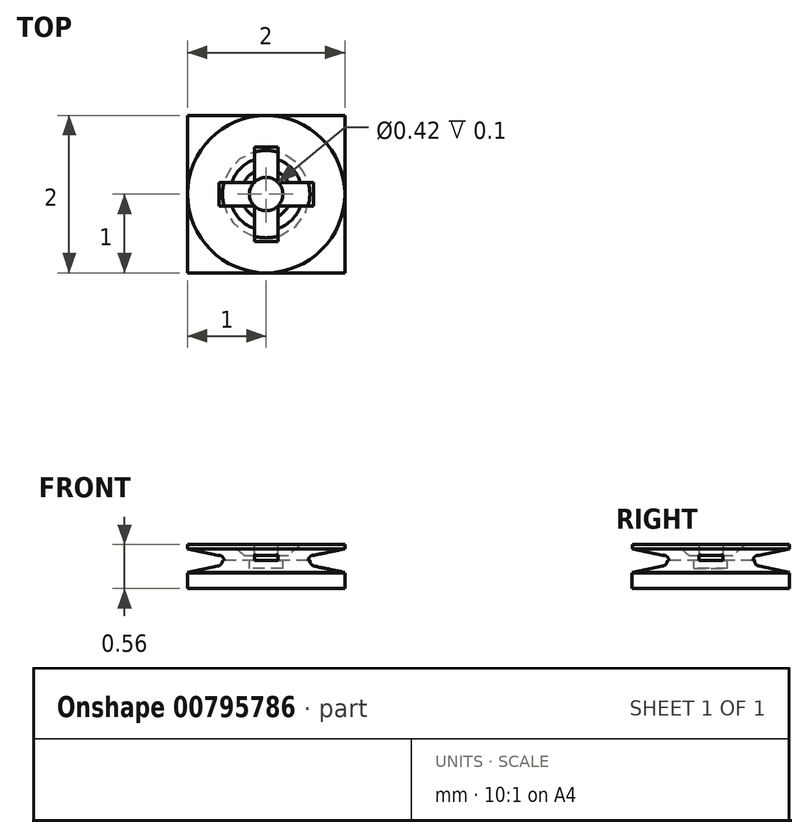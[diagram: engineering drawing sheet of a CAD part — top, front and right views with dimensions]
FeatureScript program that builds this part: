
annotation { "Feature Type Name" : "Feature", "Feature Type Description" : "" }
export const myFeature = defineFeature(function(context is Context, id is Id, definition is map)
    precondition{}
    {
        {
            var Q0;
            Q0=qCreatedBy(makeId("Top.planeOp"),FACE);
            var sketch = newSketch(context, id + "F0", { "sketchPlane" : qUnion([Q0])});
            skLineSegment(sketch, "E0.bottom", {"start": v(1, -1) * mm, "end": v(-1, -1) * mm});
            skLineSegment(sketch, "E0.top", {"start": v(1, 1) * mm, "end": v(-1, 1) * mm});
            skLineSegment(sketch, "E0.left", {"start": v(1, -1) * mm, "end": v(1, 1) * mm});
            skLineSegment(sketch, "E0.right", {"start": v(-1, -1) * mm, "end": v(-1, 1) * mm});
            skPoint(sketch, "E0.middle", {"position": v(0, 0) * mm});
            skSolve(sketch);
        }
        {
            var Q0;
            Q0 = qSketchRegion(id + "F0", true);
            extrude(context, id + "F1", {"entities" : qUnion([Q0]), "depth" : 0.2 * mm, "offsetDistance" : 25 * mm});
        }
        {
            var Q0;
            Q0=qCreatedBy(makeId("Right.planeOp"),FACE);
            var sketch = newSketch(context, id + "F2", { "sketchPlane" : qUnion([Q0])});
            skLineSegment(sketch, "E1", {"start": v(-1, 0.2) * mm, "end": v(-0.61, 0.28) * mm});
            skArc(sketch, "E2", {"start": v(-0.61, 0.28) * mm, "mid": v(-0.55, 0.35) * mm, "end": v(-0.61, 0.42) * mm});
            skLineSegment(sketch, "E3", {"start": v(-0.32, 0.42) * mm, "end": v(0, 0.42) * mm});
            skLineSegment(sketch, "E4", {"start": v(0, 0.42) * mm, "end": v(0, 0.2) * mm});
            skLineSegment(sketch, "E5", {"start": v(0, 0.2) * mm, "end": v(-1, 0.2) * mm});
            skLineSegment(sketch, "E6", {"start": v(-0.61, 0.42) * mm, "end": v(-1, 0.5) * mm});
            skLineSegment(sketch, "E7", {"start": v(-1, 0.5) * mm, "end": v(-1, 0.56) * mm});
            skLineSegment(sketch, "E8", {"start": v(-1, 0.56) * mm, "end": v(-0.46, 0.56) * mm});
            skLineSegment(sketch, "E9", {"start": v(-0.32, 0.42) * mm, "end": v(-0.46, 0.56) * mm});
            skSolve(sketch);
        }
        {
            var Q0;
            Q0=makeQuery(id+"F2.imprint","IMPRINT",FACE,{"disambiguationData":[TD([[makeQuery(id+"F2.imprint","IMPRINT",EDGE,{"derivedFrom":sQuery(id+"F2.wireOp",EDGE,"E1")}),-1.0]])]});
            var Q1;
            Q1=sQuery(id+"F2.wireOp",EDGE,"E4");
            revolve(context, id + "F3", {"surfaceOperationType" : NewSurfaceOperationType.NEW, "entities" : qUnion([Q0]), "axis" : qUnion([Q1]), "revolveType" : RevolveType.FULL});
        }
        {
            var Q0;
            Q0=makeQuery(id+"F3.opRevolve","SWEPT_FACE",FACE,{"disambiguationData":[OSD([sQuery(id+"F2.wireOp",EDGE,"E8")])]});
            var sketch = newSketch(context, id + "F4", { "sketchPlane" : qUnion([Q0])});
            skLineSegment(sketch, "E10.bottom", {"start": v(0.6, 0.15) * mm, "end": v(-0.6, 0.15) * mm});
            skLineSegment(sketch, "E10.top", {"start": v(0.6, -0.15) * mm, "end": v(-0.6, -0.15) * mm});
            skLineSegment(sketch, "E10.left", {"start": v(0.6, 0.15) * mm, "end": v(0.6, -0.15) * mm});
            skLineSegment(sketch, "E10.right", {"start": v(-0.6, 0.15) * mm, "end": v(-0.6, -0.15) * mm});
            skPoint(sketch, "E10.middle", {"position": v(0, 0) * mm});
            skLineSegment(sketch, "E11.bottom", {"start": v(0.15, 0.6) * mm, "end": v(-0.15, 0.6) * mm});
            skLineSegment(sketch, "E11.top", {"start": v(0.15, -0.6) * mm, "end": v(-0.15, -0.6) * mm});
            skLineSegment(sketch, "E11.left", {"start": v(0.15, 0.6) * mm, "end": v(0.15, -0.6) * mm});
            skLineSegment(sketch, "E11.right", {"start": v(-0.15, 0.6) * mm, "end": v(-0.15, -0.6) * mm});
            skSolve(sketch);
        }
        {
            var Q0;
            {var subQ0=sQuery(id+"F4.wireOp",EDGE,"E11.top");Q0=makeQuery(id+"F4.imprint","IMPRINT",FACE,{"disambiguationData":[TD([[makeQuery(id+"F4.imprint","IMPRINT",EDGE,{"derivedFrom":subQ0}),-1.0]])]});}
            var Q1;
            {var subQ0=sQuery(id+"F4.wireOp",EDGE,"E11.left");var subQ1=sQuery(id+"F4.wireOp",EDGE,"E10.top");var subQ2=makeQuery(id+"F4.imprint","INTERSECT",VERTEX,{"derivedFrom":[subQ1,subQ0]});Q1=makeQuery(id+"F4.imprint","IMPRINT",FACE,{"disambiguationData":[TD([[makeQuery(id+"F4.imprint","IMPRINT",EDGE,{"disambiguationData":[TD([[subQ2,-1.0]])],"derivedFrom":subQ1}),1.0]])]});}
            var Q2;
            {var subQ0=sQuery(id+"F4.wireOp",EDGE,"E11.left");var subQ1=sQuery(id+"F4.wireOp",EDGE,"E10.bottom");var subQ2=makeQuery(id+"F4.imprint","INTERSECT",VERTEX,{"derivedFrom":[subQ1,subQ0]});Q2=makeQuery(id+"F4.imprint","IMPRINT",FACE,{"disambiguationData":[TD([[makeQuery(id+"F4.imprint","IMPRINT",EDGE,{"disambiguationData":[TD([[subQ2,-1.0]])],"derivedFrom":subQ1}),1.0]])]});}
            var Q3;
            {var subQ0=sQuery(id+"F4.wireOp",EDGE,"E11.left");var subQ1=sQuery(id+"F4.wireOp",EDGE,"E10.bottom");var subQ2=makeQuery(id+"F4.imprint","INTERSECT",VERTEX,{"derivedFrom":[subQ1,subQ0]});Q3=makeQuery(id+"F4.imprint","IMPRINT",FACE,{"disambiguationData":[TD([[makeQuery(id+"F4.imprint","IMPRINT",EDGE,{"disambiguationData":[TD([[subQ2,-1.0]])],"derivedFrom":subQ1}),-1.0]])]});}
            var Q4;
            {var subQ0=sQuery(id+"F4.wireOp",EDGE,"E11.bottom");Q4=makeQuery(id+"F4.imprint","IMPRINT",FACE,{"disambiguationData":[TD([[makeQuery(id+"F4.imprint","IMPRINT",EDGE,{"derivedFrom":subQ0}),1.0]])]});}
            var Q5;
            {var subQ0=sQuery(id+"F4.wireOp",EDGE,"E11.left");var subQ1=sQuery(id+"F4.wireOp",EDGE,"E10.bottom");var subQ2=makeQuery(id+"F4.imprint","INTERSECT",VERTEX,{"derivedFrom":[subQ1,subQ0]});Q5=makeQuery(id+"F4.imprint","IMPRINT",FACE,{"disambiguationData":[TD([[makeQuery(id+"F4.imprint","IMPRINT",EDGE,{"disambiguationData":[TD([[subQ2,-1.0]])],"derivedFrom":subQ0}),1.0]])]});}
            var Q6;
            {var subQ0=sQuery(id+"F4.wireOp",EDGE,"E10.left");Q6=makeQuery(id+"F4.imprint","IMPRINT",FACE,{"disambiguationData":[TD([[makeQuery(id+"F4.imprint","IMPRINT",EDGE,{"derivedFrom":subQ0}),-1.0]])]});}
            var Q7;
            {var subQ0=sQuery(id+"F4.wireOp",EDGE,"E10.right");Q7=makeQuery(id+"F4.imprint","IMPRINT",FACE,{"disambiguationData":[TD([[makeQuery(id+"F4.imprint","IMPRINT",EDGE,{"derivedFrom":subQ0}),1.0]])]});}
            var Q8;
            {var subQ0=sQuery(id+"F4.wireOp",EDGE,"E11.right");var subQ1=sQuery(id+"F4.wireOp",EDGE,"E10.bottom");var subQ2=makeQuery(id+"F4.imprint","INTERSECT",VERTEX,{"derivedFrom":[subQ1,subQ0]});Q8=makeQuery(id+"F4.imprint","IMPRINT",FACE,{"disambiguationData":[TD([[makeQuery(id+"F4.imprint","IMPRINT",EDGE,{"disambiguationData":[TD([[subQ2,-1.0]])],"derivedFrom":subQ0}),-1.0]])]});}
            extrude(context, id + "F5", {"entities" : qUnion([Q0, Q1, Q2, Q3, Q4, Q5, Q6, Q7, Q8]), "operationType" : NewBodyOperationType.REMOVE, "oppositeDirection" : true, "depth" : 0.2 * mm, "offsetDistance" : 25 * mm});
        }
        {
            var Q0;
            Q0=makeQuery(id+"F5.boolean.opBoolean","COPY",FACE,{"derivedFrom":makeQuery(id+"F5.opExtrude","CAP_FACE",FACE,{"disambiguationData":[OSD([sQuery(id+"F4.wireOp",EDGE,"E10.bottom"),sQuery(id+"F4.wireOp",EDGE,"E10.top"),sQuery(id+"F4.wireOp",EDGE,"E10.left"),sQuery(id+"F4.wireOp",EDGE,"E10.right"),sQuery(id+"F4.wireOp",EDGE,"E11.bottom"),sQuery(id+"F4.wireOp",EDGE,"E11.top"),sQuery(id+"F4.wireOp",EDGE,"E11.left"),sQuery(id+"F4.wireOp",EDGE,"E11.right")])],"isStart":false})});
            var sketch = newSketch(context, id + "F6", { "sketchPlane" : qUnion([Q0])});
            skCircle(sketch, "E12", {"center": v(0, 0) * mm, "radius": 0.21 * mm});
            skSolve(sketch);
        }
        {
            var Q0;
            {var subQ0=sQuery(id+"F6.wireOp",EDGE,"E12");var subQ1=sQuery(id+"F4.wireOp",EDGE,"E11.left");var subQ2=sQuery(id+"F4.wireOp",EDGE,"E10.bottom");var subQ3=makeQuery(id+"F4.imprint","INTERSECT",VERTEX,{"derivedFrom":[subQ2,subQ1]});var subQ6=sQuery(id+"F4.wireOp",EDGE,"E11.bottom");var subQ8=sQuery(id+"F4.wireOp",EDGE,"E10.left");var subQ9=makeQuery(id+"F6.imprint","INTERSECT",VERTEX,{"derivedFrom":[makeQuery(id+"F5.boolean.opBoolean","COPY",EDGE,{"derivedFrom":makeQuery(id+"F5.opExtrude","CAP_EDGE",EDGE,{"disambiguationData":[OSD([subQ2]),TDD([makeQuery(id+"F4.imprint","IMPRINT",EDGE,{"disambiguationData":[TD([[makeQuery(id+"F4.imprint","INTERSECT",VERTEX,{"derivedFrom":[subQ2,subQ8]}),-1.0]])],"derivedFrom":subQ2}),makeQuery(id+"F4.imprint","IMPRINT",EDGE,{"disambiguationData":[TD([[subQ3,1.0]])],"derivedFrom":subQ2})])],"isStart":false})}),makeQuery(id+"F5.boolean.opBoolean","COPY",EDGE,{"derivedFrom":makeQuery(id+"F5.opExtrude","CAP_EDGE",EDGE,{"disambiguationData":[OSD([subQ1]),TDD([makeQuery(id+"F4.imprint","IMPRINT",EDGE,{"disambiguationData":[TD([[makeQuery(id+"F4.imprint","INTERSECT",VERTEX,{"derivedFrom":[subQ6,subQ1]}),-1.0]])],"derivedFrom":subQ1}),makeQuery(id+"F4.imprint","IMPRINT",EDGE,{"disambiguationData":[TD([[subQ3,1.0]])],"derivedFrom":subQ1})])],"isStart":false})}),subQ0]});Q0=makeQuery(id+"F6.imprint","IMPRINT",FACE,{"disambiguationData":[TD([[makeQuery(id+"F6.imprint","IMPRINT",EDGE,{"disambiguationData":[TD([[subQ9,-1.0]])],"derivedFrom":subQ0}),1.0]])]});}
            extrude(context, id + "F7", {"entities" : qUnion([Q0]), "operationType" : NewBodyOperationType.REMOVE, "oppositeDirection" : true, "depth" : 0.1 * mm, "offsetDistance" : 25 * mm});
        }
    });
